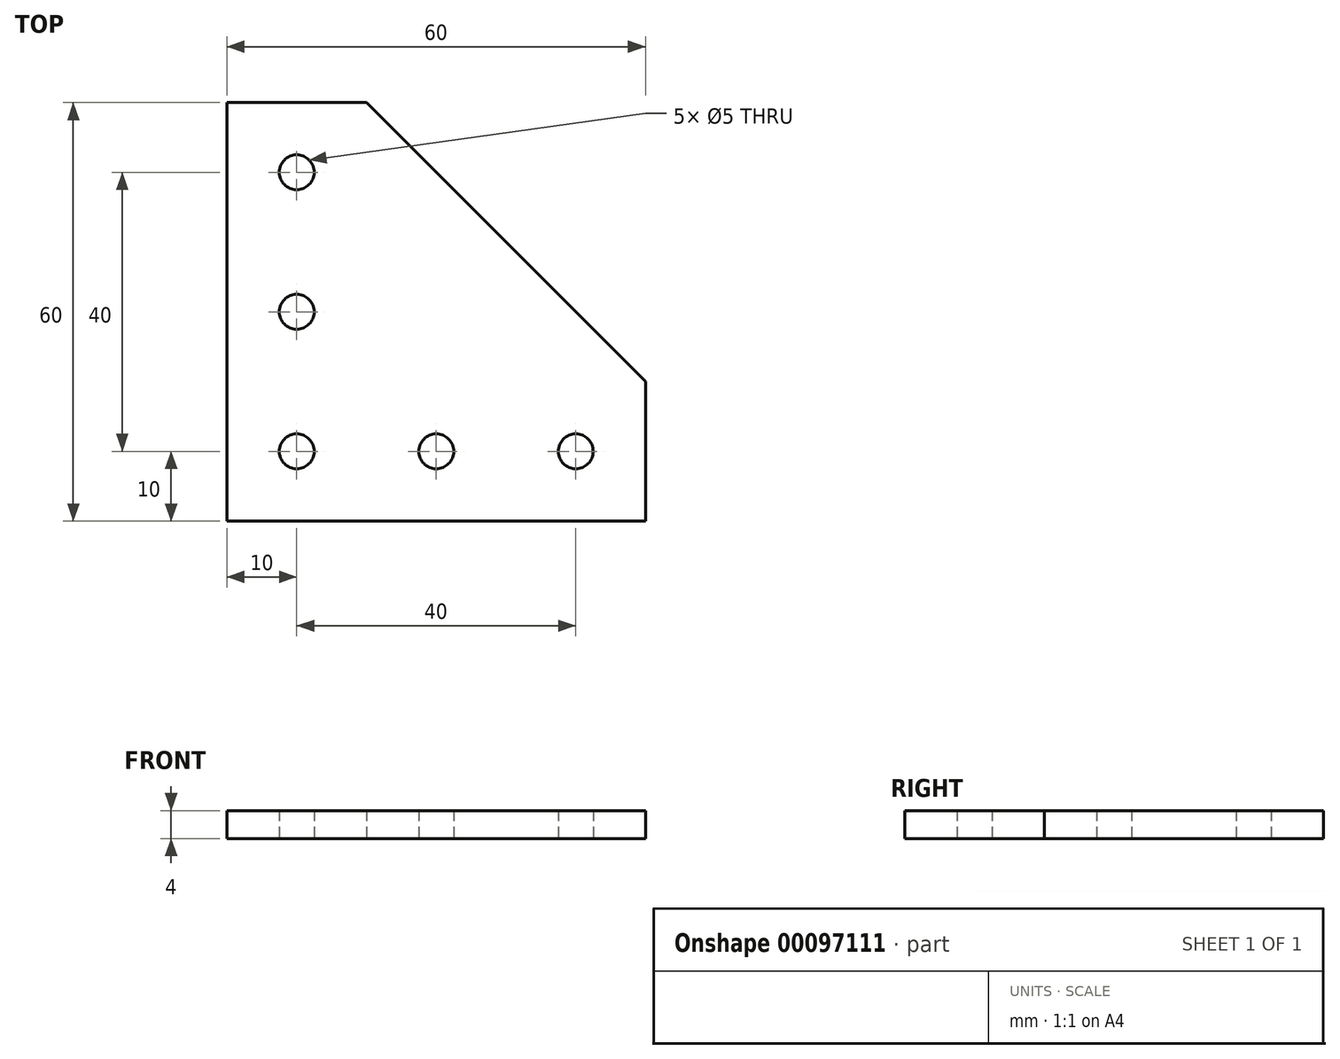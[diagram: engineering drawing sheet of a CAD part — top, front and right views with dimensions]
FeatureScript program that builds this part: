
annotation { "Feature Type Name" : "Feature", "Feature Type Description" : "" }
export const myFeature = defineFeature(function(context is Context, id is Id, definition is map)
    precondition{}
    {
        {
            var Q0;
            Q0=qCreatedBy(makeId("Top.planeOp"),FACE);
            var sketch = newSketch(context, id + "F0", { "sketchPlane" : qUnion([Q0])});
            skLineSegment(sketch, "E0", {"start": v(0, 0) * mm, "end": v(60, 0) * mm});
            skLineSegment(sketch, "E1", {"start": v(60, 0) * mm, "end": v(60, 20) * mm});
            skLineSegment(sketch, "E2", {"start": v(60, 20) * mm, "end": v(20, 60) * mm});
            skLineSegment(sketch, "E3", {"start": v(20, 60) * mm, "end": v(0, 60) * mm});
            skLineSegment(sketch, "E4", {"start": v(0, 60) * mm, "end": v(0, 0) * mm});
            skCircle(sketch, "E5", {"center": v(10, 50) * mm, "radius": 2.5 * mm});
            skCircle(sketch, "E6", {"center": v(10, 30) * mm, "radius": 2.5 * mm});
            skCircle(sketch, "E7", {"center": v(10, 10) * mm, "radius": 2.5 * mm});
            skCircle(sketch, "E8", {"center": v(30, 10) * mm, "radius": 2.5 * mm});
            skCircle(sketch, "E9", {"center": v(50, 10) * mm, "radius": 2.5 * mm});
            skSolve(sketch);
        }
        {
            var Q0;
            Q0=qSketchRegion(id+"F0",true);
            extrude(context, id + "F1", {"entities" : qUnion([Q0]), "depth" : 4 * mm});
        }
    });
